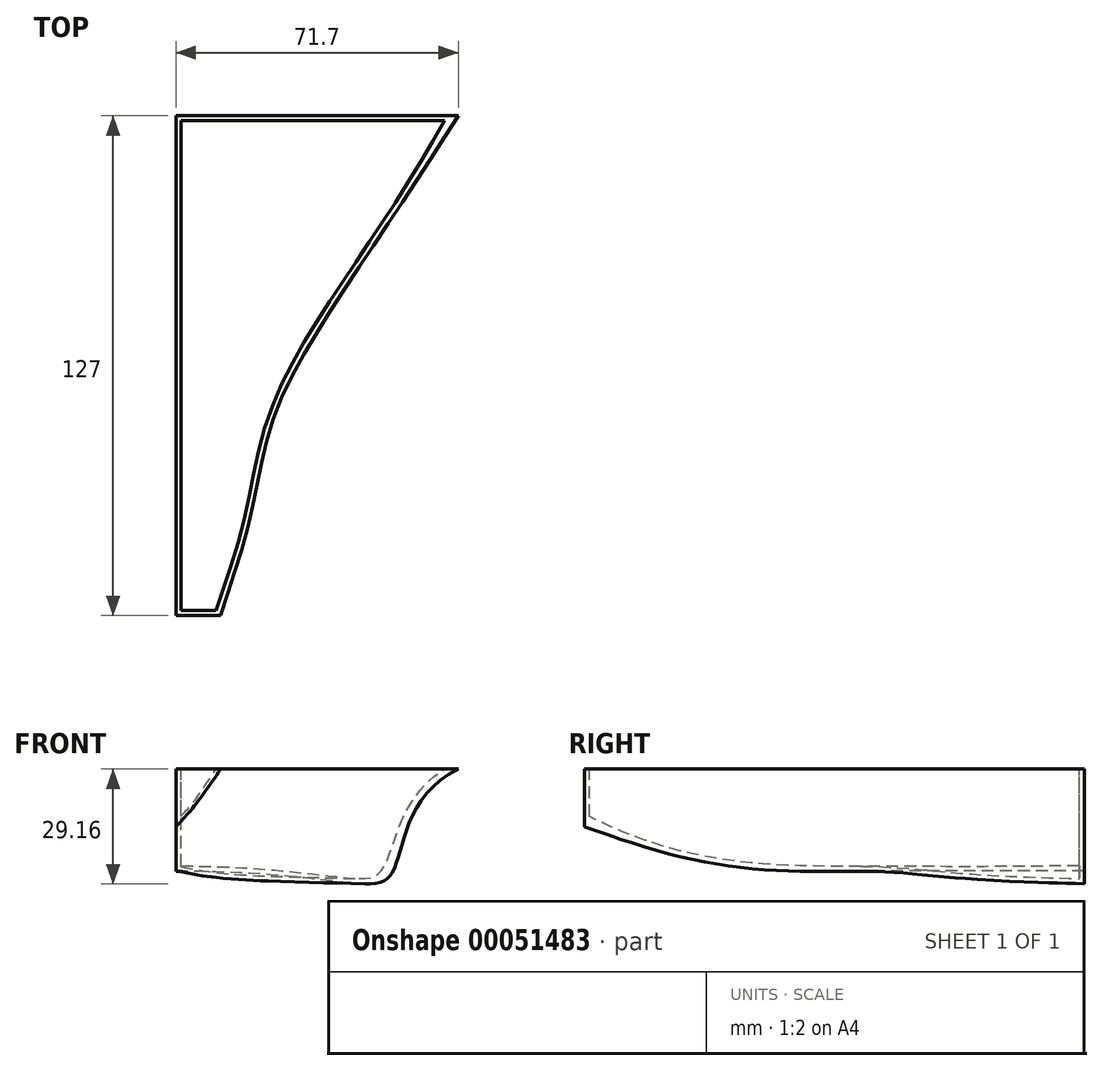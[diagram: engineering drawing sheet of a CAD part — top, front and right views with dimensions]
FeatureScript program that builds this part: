
annotation { "Feature Type Name" : "Feature", "Feature Type Description" : "" }
export const myFeature = defineFeature(function(context is Context, id is Id, definition is map)
    precondition{}
    {
        {
            var Q0;
            Q0=qCreatedBy(makeId("Front.planeOp"),FACE);
            var sketch = newSketch(context, id + "F0", { "sketchPlane" : qUnion([Q0])});
            skFitSpline(sketch, "E0", {"points": [v(0, 0) * mm, v(55.16, 0) * mm, v(71.7, 25.87) * mm], "startDerivative": vector(224.94, 0) * mm, "endDerivative": vector(95.08, 46.11) * mm});
            skLineSegment(sketch, "E1", {"start": v(71.7, 25.87) * mm, "end": v(0, 25.87) * mm});
            skLineSegment(sketch, "E2", {"start": v(0, 25.87) * mm, "end": v(0, 0) * mm});
            skSolve(sketch);
        }
        {
            var Q0;
            Q0=qCreatedBy(makeId("Front.planeOp"),FACE);
            cPlane(context, id + "F1", {"entities" : qUnion([Q0]), "cplaneType" : CPlaneType.OFFSET, "offset" : 25.4 * mm, "width" : 152.4 * mm, "height" : 152.4 * mm});
        }
        {
            var Q0;
            Q0=qCreatedBy(makeId("Front.planeOp"),FACE);
            cPlane(context, id + "F2", {"entities" : qUnion([Q0]), "cplaneType" : CPlaneType.OFFSET, "offset" : 50.8 * mm, "width" : 152.4 * mm, "height" : 152.4 * mm});
        }
        {
            var Q0;
            Q0=qCreatedBy(makeId("Front.planeOp"),FACE);
            cPlane(context, id + "F3", {"entities" : qUnion([Q0]), "cplaneType" : CPlaneType.OFFSET, "offset" : 76.2 * mm, "width" : 152.4 * mm, "height" : 152.4 * mm});
        }
        {
            var Q0;
            Q0=qCreatedBy(makeId("Front.planeOp"),FACE);
            cPlane(context, id + "F4", {"entities" : qUnion([Q0]), "cplaneType" : CPlaneType.OFFSET, "offset" : 101.6 * mm, "width" : 152.4 * mm, "height" : 152.4 * mm});
        }
        {
            var Q0;
            Q0=qCreatedBy(id+"F1.planeOp",FACE);
            var sketch = newSketch(context, id + "F5", { "sketchPlane" : qUnion([Q0])});
            skLineSegment(sketch, "E3.0", {"start": v(0, 25.87) * mm, "end": v(0, 0) * mm, "construction": true});
            skLineSegment(sketch, "E4.0", {"start": v(55.24, 25.87) * mm, "end": v(0, 25.87) * mm, "construction": true});
            skFitSpline(sketch, "E5", {"points": [v(0, 0) * mm, v(31.62, 0) * mm, v(55.24, 25.87) * mm], "startDerivative": vector(69.49, -12.29) * mm, "endDerivative": vector(41.23, 63.39) * mm});
            skLineSegment(sketch, "E6.0", {"start": v(55.24, 25.87) * mm, "end": v(0, 25.87) * mm});
            skLineSegment(sketch, "E7.0", {"start": v(0, 25.87) * mm, "end": v(0, 0) * mm});
            skPoint(sketch, "E8.orphan", {"position": v(71.7, 25.87) * mm});
            skSolve(sketch);
        }
        {
            var Q0;
            Q0=qCreatedBy(id+"F2.planeOp",FACE);
            var sketch = newSketch(context, id + "F6", { "sketchPlane" : qUnion([Q0])});
            skLineSegment(sketch, "E9.0", {"start": v(38.46, 25.87) * mm, "end": v(0, 25.87) * mm});
            skLineSegment(sketch, "E10.0", {"start": v(0, 25.87) * mm, "end": v(0, 0) * mm});
            skFitSpline(sketch, "E11", {"points": [v(0, 0) * mm, v(18.12, 2.28) * mm, v(38.46, 25.87) * mm], "startDerivative": vector(43.06, -2.63) * mm, "endDerivative": vector(34.24, 51.96) * mm});
            skPoint(sketch, "E12.orphan", {"position": v(55.24, 25.87) * mm});
            skSolve(sketch);
        }
        {
            var Q0;
            Q0=qCreatedBy(id+"F3.planeOp",FACE);
            var sketch = newSketch(context, id + "F7", { "sketchPlane" : qUnion([Q0])});
            skLineSegment(sketch, "E13.0", {"start": v(25.04, 25.87) * mm, "end": v(0, 25.87) * mm});
            skLineSegment(sketch, "E14.0", {"start": v(0, 25.87) * mm, "end": v(0, 0) * mm});
            skFitSpline(sketch, "E15", {"points": [v(0, 0) * mm, v(11.02, 3.82) * mm, v(25.04, 25.87) * mm], "startDerivative": vector(28.35, 4.07) * mm, "endDerivative": vector(22.13, 44.96) * mm});
            skPoint(sketch, "E16.orphan", {"position": v(38.46, 25.87) * mm});
            skSolve(sketch);
        }
        {
            var Q0;
            Q0=qCreatedBy(makeId("Front.planeOp"),FACE);
            cPlane(context, id + "F8", {"entities" : qUnion([Q0]), "cplaneType" : CPlaneType.OFFSET, "offset" : 127 * mm, "width" : 152.4 * mm, "height" : 152.4 * mm});
        }
        {
            var Q0;
            Q0=qCreatedBy(makeId("Front.planeOp"),FACE);
            cPlane(context, id + "F9", {"entities" : qUnion([Q0]), "cplaneType" : CPlaneType.OFFSET, "offset" : 152.4 * mm, "width" : 152.4 * mm, "height" : 152.4 * mm});
        }
        {
            var Q0;
            Q0=qCreatedBy(id+"F4.planeOp",FACE);
            var sketch = newSketch(context, id + "F10", { "sketchPlane" : qUnion([Q0])});
            skLineSegment(sketch, "E17.0", {"start": v(0, 25.87) * mm, "end": v(0, 3.32) * mm});
            skLineSegment(sketch, "E18", {"start": v(0, 25.87) * mm, "end": v(18.92, 25.87) * mm});
            skLineSegment(sketch, "E19", {"start": v(0, 25.87) * mm, "end": v(0, 0) * mm});
            skFitSpline(sketch, "E20", {"points": [v(0, 3.32) * mm, v(8.18, 6.22) * mm, v(18.92, 25.87) * mm], "startDerivative": vector(22.06, 2.88) * mm, "endDerivative": vector(16.23, 39.38) * mm});
            skSolve(sketch);
        }
        {
            var Q0;
            Q0=qCreatedBy(id+"F8.planeOp",FACE);
            var sketch = newSketch(context, id + "F11", { "sketchPlane" : qUnion([Q0])});
            skPoint(sketch, "E21.0", {"position": v(0, 25.87) * mm});
            skLineSegment(sketch, "E22", {"start": v(0, 25.87) * mm, "end": v(11.3, 25.87) * mm});
            skLineSegment(sketch, "E23", {"start": v(0, 25.87) * mm, "end": v(0, 11.2) * mm});
            skFitSpline(sketch, "E24", {"points": [v(0, 11.2) * mm, v(4.7, 16.53) * mm, v(11.3, 25.87) * mm], "startDerivative": vector(10.41, 11.07) * mm, "endDerivative": vector(12.13, 18) * mm});
            skSolve(sketch);
        }
        {
            var Q0;
            Q0=qCreatedBy(id+"F9.planeOp",FACE);
            var sketch = newSketch(context, id + "F12", { "sketchPlane" : qUnion([Q0])});
            skPoint(sketch, "E25.0", {"position": v(0, 25.87) * mm});
            skLineSegment(sketch, "E26", {"start": v(0, 25.87) * mm, "end": v(0, 22.82) * mm});
            skSolve(sketch);
        }
        {
            var Q0;
            Q0=makeQuery(id+"F0.imprint","IMPRINT",FACE,{"disambiguationData":[TD([[makeQuery(id+"F0.imprint","IMPRINT",EDGE,{"derivedFrom":sQuery(id+"F0.wireOp",EDGE,"E0")}),1.0]])]});
            var Q1;
            Q1=makeQuery(id+"F5.imprint","IMPRINT",FACE,{"disambiguationData":[TD([[makeQuery(id+"F5.imprint","IMPRINT",EDGE,{"derivedFrom":sQuery(id+"F5.wireOp",EDGE,"E5")}),1.0]])]});
            var Q2;
            Q2=makeQuery(id+"F6.imprint","IMPRINT",FACE,{"disambiguationData":[TD([[makeQuery(id+"F6.imprint","IMPRINT",EDGE,{"derivedFrom":sQuery(id+"F6.wireOp",EDGE,"E9.0")}),1.0]])]});
            var Q3;
            Q3=makeQuery(id+"F7.imprint","IMPRINT",FACE,{"disambiguationData":[TD([[makeQuery(id+"F7.imprint","IMPRINT",EDGE,{"derivedFrom":sQuery(id+"F7.wireOp",EDGE,"E13.0")}),1.0]])]});
            var Q4;
            {var subQ0=sQuery(id+"F10.wireOp",EDGE,"E18");Q4=makeQuery(id+"F10.imprint","IMPRINT",FACE,{"disambiguationData":[TD([[makeQuery(id+"F10.imprint","IMPRINT",EDGE,{"derivedFrom":subQ0}),-1.0]])]});}
            var Q5;
            Q5=makeQuery(id+"F11.imprint","IMPRINT",FACE,{"disambiguationData":[TD([[makeQuery(id+"F11.imprint","IMPRINT",EDGE,{"derivedFrom":sQuery(id+"F11.wireOp",EDGE,"E22")}),-1.0]])]});
            var Q6;
            Q6=sQuery(id+"F0.wireOp",EDGE,"E0");
            var Q7;
            Q7=sQuery(id+"F5.wireOp",EDGE,"E5");
            var Q8;
            Q8=sQuery(id+"F6.wireOp",EDGE,"E11");
            var Q9;
            Q9=sQuery(id+"F7.wireOp",EDGE,"E15");
            var Q10;
            Q10=sQuery(id+"F10.wireOp",EDGE,"E20");
            var Q11;
            Q11=sQuery(id+"F11.wireOp",EDGE,"E24");
            var Q12;
            Q12=sQuery(id+"F12.wireOp",EDGE,"E26");
            loft(context, id + "F13", {"sheetProfilesArray" : [{ "sheetProfileEntities" : qUnion([Q0]) }, { "sheetProfileEntities" : qUnion([Q1]) }, { "sheetProfileEntities" : qUnion([Q2]) }, { "sheetProfileEntities" : qUnion([Q3]) }, { "sheetProfileEntities" : qUnion([Q4]) }, { "sheetProfileEntities" : qUnion([Q5]) }], "wireProfilesArray" : [{ "wireProfileEntities" : qUnion([Q6]) }, { "wireProfileEntities" : qUnion([Q7]) }, { "wireProfileEntities" : qUnion([Q8]) }, { "wireProfileEntities" : qUnion([Q9]) }, { "wireProfileEntities" : qUnion([Q10]) }, { "wireProfileEntities" : qUnion([Q11]) }, { "wireProfileEntities" : qUnion([Q12]) }]});
        }
        {
            var Q0;
            {var subQ0=sQuery(id+"F5.wireOp",EDGE,"E6.0");var subQ1=sQuery(id+"F5.wireOp",EDGE,"E7.0");var subQ2=sQuery(id+"F5.wireOp",EDGE,"E5");var subQ3=sQuery(id+"F0.wireOp",EDGE,"E1");var subQ4=sQuery(id+"F0.wireOp",EDGE,"E2");var subQ5=sQuery(id+"F0.wireOp",EDGE,"E0");Q0=makeQuery(id+"F13.opLoft","SWEPT_FACE",FACE,{"disambiguationData":[OSD([subQ5,subQ3,subQ4,subQ2,subQ0,subQ1]),TDD([makeQuery(id+"F0.imprint","INTERSECT",VERTEX,{"derivedFrom":[subQ5,subQ3]}),makeQuery(id+"F0.imprint","INTERSECT",VERTEX,{"derivedFrom":[subQ3,subQ4]}),makeQuery(id+"F0.imprint","IMPRINT",EDGE,{"derivedFrom":subQ3}),makeQuery(id+"F5.imprint","INTERSECT",VERTEX,{"derivedFrom":[subQ2,subQ0]}),makeQuery(id+"F5.imprint","INTERSECT",VERTEX,{"derivedFrom":[subQ0,subQ1]}),makeQuery(id+"F5.imprint","IMPRINT",EDGE,{"derivedFrom":subQ0})])]});}
            shell(context, id + "F14", {"entities" : qUnion([Q0]), "thickness" : 1.27 * mm});
        }
    });
